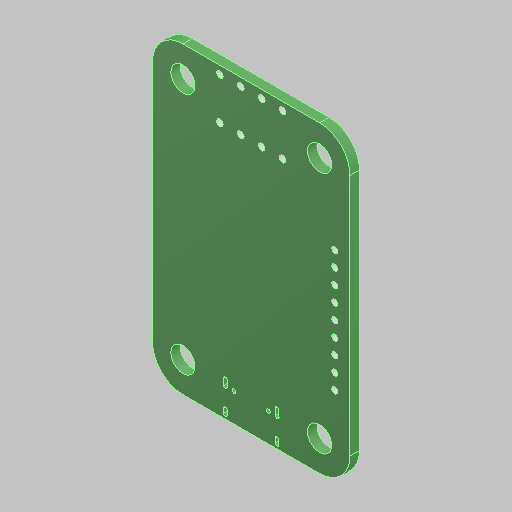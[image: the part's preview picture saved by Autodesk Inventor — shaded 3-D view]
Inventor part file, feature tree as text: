
AUTODESK INVENTOR PART (.ipt)
format: ipt  version: 2023.5 (Build 275446000, 446)  size: 145,920 bytes
history: native  units: in
note: dims shown in document units (in); Inventor stores cm internally (conversion verified against a paired STEP export)
features: fillet x1
ambient origin geometry x8: Origin, YZ Plane, XZ Plane, XY Plane, X Axis, Y Axis, Z Axis, Center Point
bodies: Solid1 (feature_tree)
feature tree (1):
  fillet  "Fillet1"  [1 undecoded]
note: 1 required parameter value undecoded (feature->parameter linkage not recoverable at this tier; creation-order binding heuristic only, values carry confidence <= 0.55)
